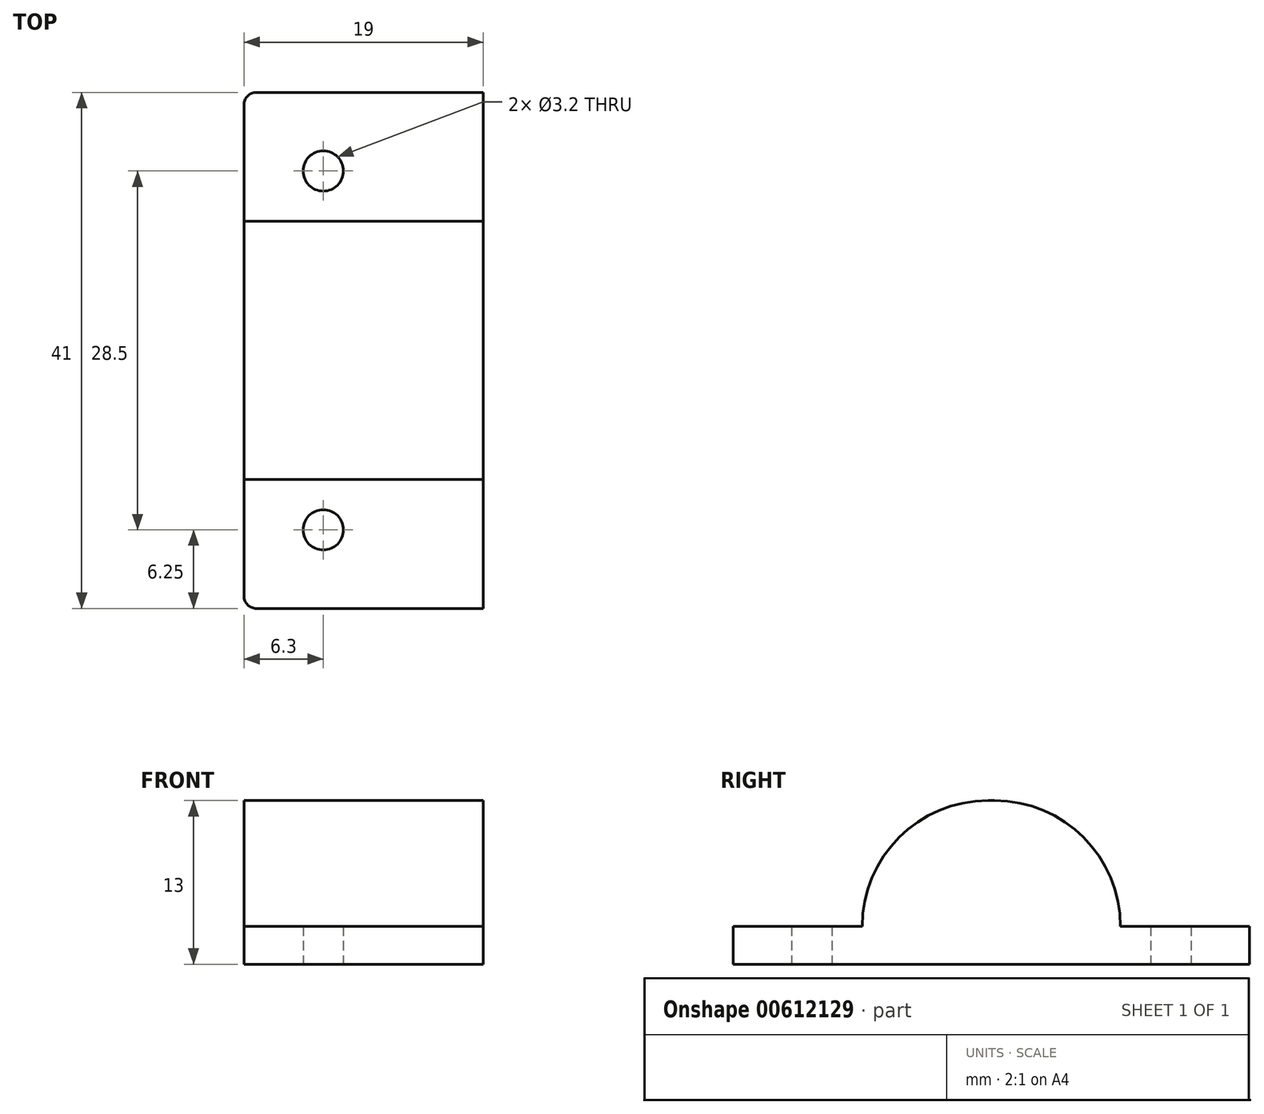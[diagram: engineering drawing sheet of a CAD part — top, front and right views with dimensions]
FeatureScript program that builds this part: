
annotation { "Feature Type Name" : "Feature", "Feature Type Description" : "" }
export const myFeature = defineFeature(function(context is Context, id is Id, definition is map)
    precondition{}
    {
        {
            var Q0;
            Q0=qCreatedBy(makeId("Top.planeOp"),FACE);
            var sketch = newSketch(context, id + "F0", { "sketchPlane" : qUnion([Q0])});
            skLineSegment(sketch, "E0.bottom", {"start": v(-19, 20.5) * mm, "end": v(0, 20.5) * mm});
            skLineSegment(sketch, "E0.top", {"start": v(-19, -20.5) * mm, "end": v(0, -20.5) * mm});
            skPoint(sketch, "E0.middle", {"position": v(0, 0) * mm});
            skLineSegment(sketch, "E1", {"start": v(-19, 20.5) * mm, "end": v(-19, -20.5) * mm});
            skCircle(sketch, "E2", {"center": v(-12.7, 14.25) * mm, "radius": 1.6 * mm});
            skCircle(sketch, "E3", {"center": v(-12.7, -14.25) * mm, "radius": 1.6 * mm});
            skLineSegment(sketch, "E4", {"start": v(0, 20.5) * mm, "end": v(0, -20.5) * mm});
            skSolve(sketch);
        }
        {
            var Q0;
            Q0 = qSketchRegion(id + "F0", true);
            extrude(context, id + "F1", {"entities" : qUnion([Q0]), "depth" : 3 * mm, "offsetDistance" : 25 * mm});
        }
        {
            var Q0;
            Q0=makeQuery(id+"F1.opExtrude","SWEPT_EDGE",EDGE,{"disambiguationData":[OSD([sQuery(id+"F0.wireOp",EDGE,"E0.top"),sQuery(id+"F0.wireOp",EDGE,"E1")])]});
            var Q1;
            Q1=makeQuery(id+"F1.opExtrude","SWEPT_EDGE",EDGE,{"disambiguationData":[OSD([sQuery(id+"F0.wireOp",EDGE,"E0.bottom"),sQuery(id+"F0.wireOp",EDGE,"E1")])]});
            fillet(context, id + "F2", {"entities" : qUnion([Q0, Q1]), "radius" : 1 * mm, "tangentPropagation" : true, "allowEdgeOverflow" : false});
        }
        {
            var Q0;
            Q0=makeQuery(id+"F1.opExtrude","CAP_FACE",FACE,{"disambiguationData":[OSD([sQuery(id+"F0.wireOp",EDGE,"E0.bottom"),sQuery(id+"F0.wireOp",EDGE,"E0.top"),sQuery(id+"F0.wireOp",EDGE,"E1"),sQuery(id+"F0.wireOp",EDGE,"E2"),sQuery(id+"F0.wireOp",EDGE,"E3"),sQuery(id+"F0.wireOp",EDGE,"E4")])],"isStart":false});
            var sketch = newSketch(context, id + "F3", { "sketchPlane" : qUnion([Q0])});
            skLineSegment(sketch, "E5", {"start": v(-19, 10.25) * mm, "end": v(0, 10.25) * mm});
            skLineSegment(sketch, "E6", {"start": v(0, 10.25) * mm, "end": v(0, -10.25) * mm});
            skLineSegment(sketch, "E7", {"start": v(0, -10.25) * mm, "end": v(-19, -10.25) * mm});
            skLineSegment(sketch, "E8", {"start": v(-19, -10.25) * mm, "end": v(-19, 10.25) * mm});
            skSolve(sketch);
        }
        {
            var Q0;
            Q0 = qSketchRegion(id + "F3", true);
            extrude(context, id + "F4", {"entities" : qUnion([Q0]), "operationType" : NewBodyOperationType.ADD, "depth" : 10 * mm, "offsetDistance" : 25 * mm});
        }
        {
            var Q0;
            Q0=makeQuery(id+"F4.opExtrude","CAP_EDGE",EDGE,{"disambiguationData":[OSD([sQuery(id+"F3.wireOp",EDGE,"E5")])],"isStart":false});
            var Q1;
            Q1=makeQuery(id+"F4.opExtrude","CAP_EDGE",EDGE,{"disambiguationData":[OSD([sQuery(id+"F3.wireOp",EDGE,"E7")])],"isStart":false});
            fillet(context, id + "F5", {"entities" : qUnion([Q0, Q1]), "radius" : 10 * mm, "tangentPropagation" : true, "allowEdgeOverflow" : false});
        }
    });
